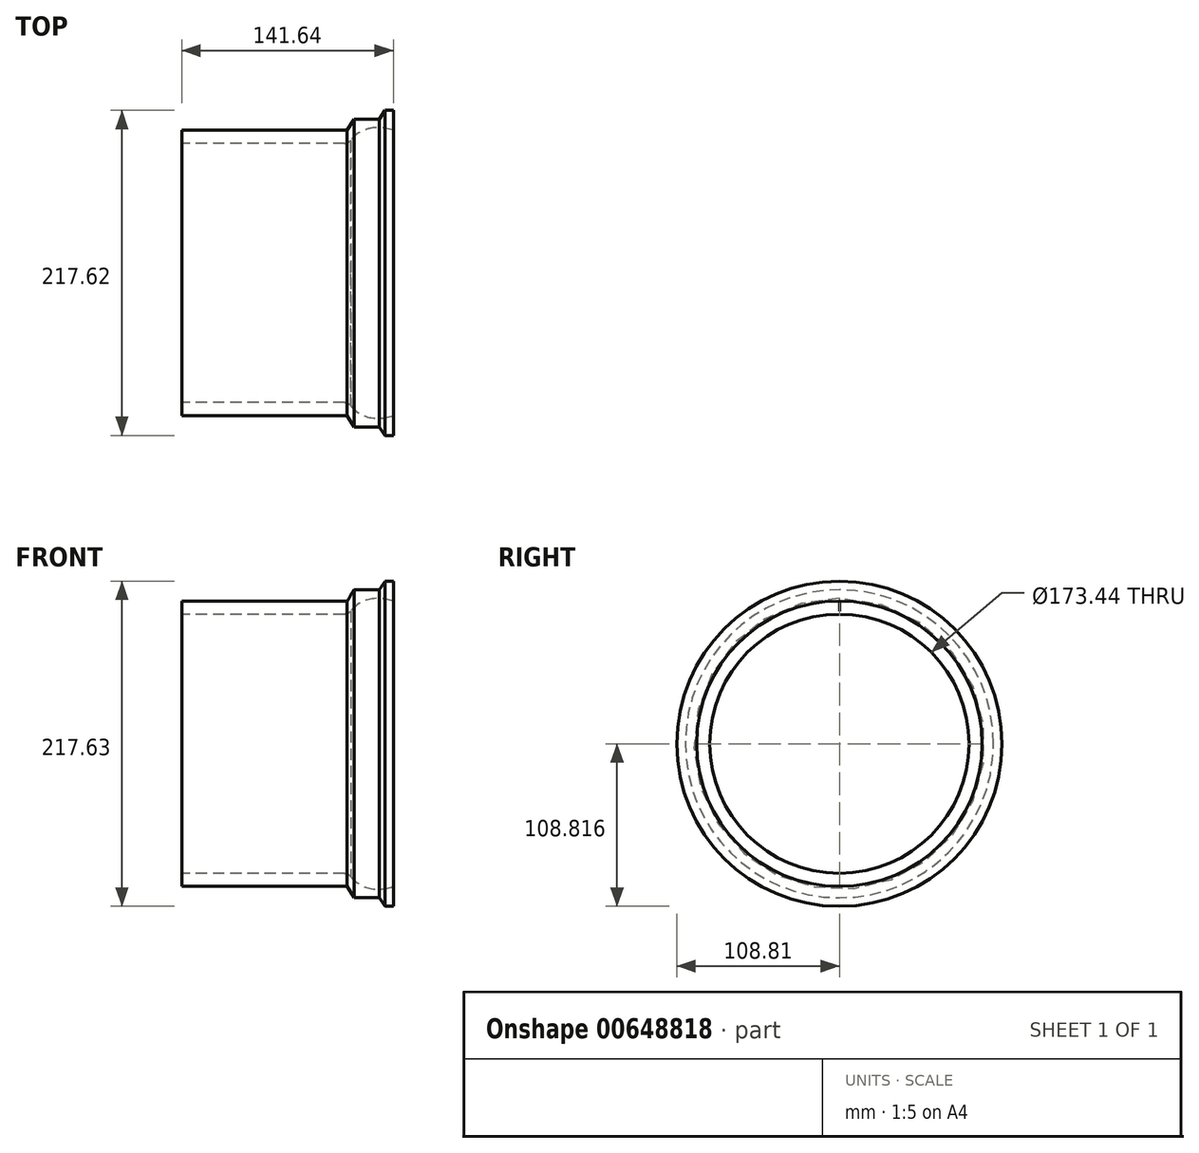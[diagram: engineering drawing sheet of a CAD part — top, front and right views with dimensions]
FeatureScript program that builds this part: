
annotation { "Feature Type Name" : "Feature", "Feature Type Description" : "" }
export const myFeature = defineFeature(function(context is Context, id is Id, definition is map)
    precondition{}
    {
        {
            var Q0;
            Q0=qCreatedBy(makeId("Front.planeOp"),FACE);
            var sketch = newSketch(context, id + "F0", { "sketchPlane" : qUnion([Q0])});
            skLineSegment(sketch, "E0", {"start": v(-93.67, 25.12) * mm, "end": v(17.1, 25.12) * mm});
            skLineSegment(sketch, "E1", {"start": v(21.64, 32.69) * mm, "end": v(38.59, 32.69) * mm});
            skLineSegment(sketch, "E2", {"start": v(38.59, 32.69) * mm, "end": v(42.52, 38.44) * mm});
            skLineSegment(sketch, "E3", {"start": v(42.52, 38.44) * mm, "end": v(47.97, 38.44) * mm});
            skLineSegment(sketch, "E4", {"start": v(17.1, 25.12) * mm, "end": v(21.64, 32.69) * mm});
            skLineSegment(sketch, "E5", {"start": v(47.97, 38.44) * mm, "end": v(47.97, 25.12) * mm});
            skFitSpline(sketch, "E6", {"points": [v(47.97, 25.12) * mm, v(18, 16.34) * mm], "startDerivative": vector(-28.15, 9.37) * mm, "endDerivative": vector(-21.96, -35.7) * mm});
            skLineSegment(sketch, "E7", {"start": v(18, 16.34) * mm, "end": v(-93.09, 16.34) * mm});
            skLineSegment(sketch, "E8", {"start": v(-93.67, 25.12) * mm, "end": v(-93.09, 16.34) * mm});
            skLineSegment(sketch, "E9", {"start": v(-158.6, -70.37) * mm, "end": v(139.06, -70.37) * mm});
            skSolve(sketch);
        }
        {
            var Q0;
            Q0=makeQuery(id+"F0.imprint","IMPRINT",FACE,{"disambiguationData":[TD([[makeQuery(id+"F0.imprint","IMPRINT",EDGE,{"derivedFrom":sQuery(id+"F0.wireOp",EDGE,"E0")}),-1.0]])]});
            var Q1;
            Q1=sQuery(id+"F0.wireOp",EDGE,"E9");
            revolve(context, id + "F1", {"entities" : qUnion([Q0]), "axis" : qUnion([Q1]), "revolveType" : RevolveType.FULL});
        }
        {
            var Q0;
            Q0=makeQuery(id+"F1.opRevolve","SWEPT_EDGE",EDGE,{"disambiguationData":[OSD([sQuery(id+"F0.wireOp",EDGE,"E6"),sQuery(id+"F0.wireOp",EDGE,"E7")])]});
            fillet(context, id + "F2", {"entities" : qUnion([Q0]), "radius" : 5.08 * mm, "tangentPropagation" : true, "allowEdgeOverflow" : false});
        }
    });
